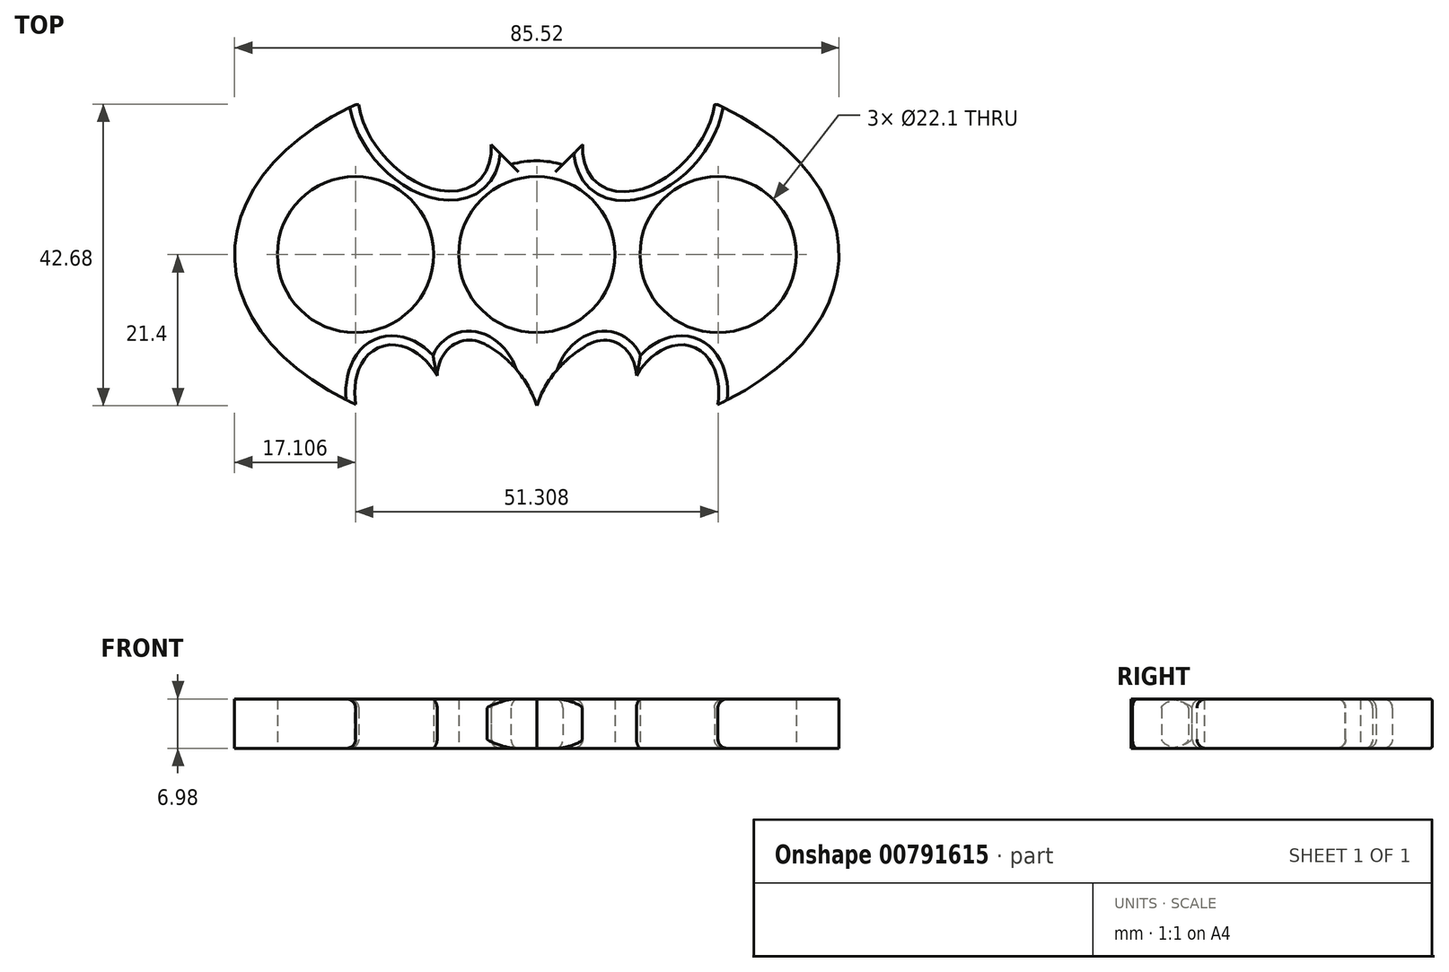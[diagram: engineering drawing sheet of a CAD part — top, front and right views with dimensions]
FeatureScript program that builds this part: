
annotation { "Feature Type Name" : "Feature", "Feature Type Description" : "" }
export const myFeature = defineFeature(function(context is Context, id is Id, definition is map)
    precondition{}
    {
        {
            var Q0;
            Q0=qCreatedBy(makeId("Top.planeOp"),FACE);
            var sketch = newSketch(context, id + "F0", { "sketchPlane" : qUnion([Q0])});
            skCircle(sketch, "E0", {"center": v(0, 0) * mm, "radius": 11.05 * mm});
            skCircle(sketch, "E1", {"center": v(25.65, 0) * mm, "radius": 11.05 * mm});
            skCircle(sketch, "E2", {"center": v(-25.65, 0) * mm, "radius": 11.05 * mm});
            skEllipse(sketch, "E3", {"center": v(0, 0) * mm, "majorRadius": 42.76 * mm, "minorRadius": 26.5 * mm, "majorAxis": v(1, 0)});
            skPoint(sketch, "E4", {"position": v(0, 11.05) * mm});
            skPoint(sketch, "E5", {"position": v(-25.65, 21.2) * mm});
            skLineSegment(sketch, "E6", {"start": v(-25.65, 21.2) * mm, "end": v(25.65, 21.2) * mm});
            skPoint(sketch, "E7", {"position": v(0, 21.2) * mm});
            skPoint(sketch, "E8", {"position": v(-24.47, -10.99) * mm});
            skPoint(sketch, "E9", {"position": v(1.18, -10.99) * mm});
            skPoint(sketch, "E10", {"position": v(26.84, -10.99) * mm});
            skLineSegment(sketch, "E11", {"start": v(-24.47, -10.99) * mm, "end": v(1.18, -10.99) * mm});
            skLineSegment(sketch, "E12", {"start": v(26.84, -10.99) * mm, "end": v(1.18, -10.99) * mm});
            skLineSegment(sketch, "E13", {"start": v(0, 0) * mm, "end": v(-19.73, 23.51) * mm});
            skLineSegment(sketch, "E14", {"start": v(0, 0) * mm, "end": v(19.73, 23.51) * mm});
            skEllipse(sketch, "E15", {"center": v(-15.88, 18.92) * mm, "majorRadius": 11.43 * mm, "minorRadius": 7.62 * mm, "majorAxis": v(0.66, -0.75)});
            skPoint(sketch, "E16", {"position": v(15.87, 18.92) * mm});
            skEllipse(sketch, "E17", {"center": v(15.87, 18.92) * mm, "majorRadius": 11.43 * mm, "minorRadius": 7.62 * mm, "majorAxis": v(-0.64, -0.77)});
            skCircle(sketch, "E18", {"center": v(0, 0) * mm, "radius": 13.26 * mm});
            skLineSegment(sketch, "E19", {"start": v(-6.43, 15.55) * mm, "end": v(6.5, 15.55) * mm});
            skLineSegment(sketch, "E20", {"start": v(-6.43, 15.55) * mm, "end": v(-3.63, 12.76) * mm});
            skLineSegment(sketch, "E21", {"start": v(6.5, 15.55) * mm, "end": v(3.69, 12.74) * mm});
            skLineSegment(sketch, "E22", {"start": v(-25.24, 21.4) * mm, "end": v(0, 21.4) * mm});
            skLineSegment(sketch, "E23", {"start": v(0, 26.5) * mm, "end": v(-1.53, 26.5) * mm});
            skPoint(sketch, "E24", {"position": v(0, -21.4) * mm});
            skLineSegment(sketch, "E25", {"start": v(0, -26.5) * mm, "end": v(1.19, -26.5) * mm});
            skLineSegment(sketch, "E26", {"start": v(0, -21.4) * mm, "end": v(-25.24, -21.4) * mm});
            skLineSegment(sketch, "E27", {"start": v(-25.24, -21.4) * mm, "end": v(0, -21.4) * mm});
            skLineSegment(sketch, "E28", {"start": v(25.24, -21.4) * mm, "end": v(0, -21.4) * mm});
            skEllipse(sketch, "E29", {"center": v(-19.05, -21.4) * mm, "majorRadius": 8.9 * mm, "minorRadius": 6.35 * mm, "majorAxis": v(0.34, -0.94)});
            skEllipse(sketch, "E30", {"center": v(-8.9, -18.35) * mm, "majorRadius": 6.35 * mm, "minorRadius": 5.08 * mm, "majorAxis": v(0.3, -0.95)});
            skArc(sketch, "E31", {"start": v(0, -21.4) * mm, "mid": v(-2.93, -16.21) * mm, "end": v(-7.62, -12.55) * mm});
            skEllipse(sketch, "E32", {"center": v(8.89, -18.35) * mm, "majorRadius": 6.35 * mm, "minorRadius": 5.08 * mm, "majorAxis": v(0.3, 0.95)});
            skEllipse(sketch, "E33", {"center": v(19.05, -21.4) * mm, "majorRadius": 8.9 * mm, "minorRadius": 6.35 * mm, "majorAxis": v(0.34, 0.94)});
            skArc(sketch, "E34", {"start": v(6.41, -13.3) * mm, "mid": v(2.5, -16.78) * mm, "end": v(0, -21.4) * mm});
            skLineSegment(sketch, "E35", {"start": v(19.05, -21.4) * mm, "end": v(22.1, -13.04) * mm});
            skLineSegment(sketch, "E36", {"start": v(-8.9, -18.35) * mm, "end": v(8.9, -18.35) * mm});
            skLineSegment(sketch, "E37", {"start": v(-8.9, -18.35) * mm, "end": v(-10.85, -12.3) * mm});
            skLineSegment(sketch, "E38", {"start": v(8.9, -18.35) * mm, "end": v(10.85, -12.3) * mm});
            skLineSegment(sketch, "E39", {"start": v(-19.05, -21.4) * mm, "end": v(-22.1, -13.04) * mm});
            skSolve(sketch);
        }
        {
            var Q0;
            Q0=makeQuery(id+"F0.imprint","IMPRINT",FACE,{"disambiguationData":[TD([[makeQuery(id+"F0.imprint","IMPRINT",EDGE,{"derivedFrom":sQuery(id+"F0.wireOp",EDGE,"E2")}),-1.0]])]});
            var Q1;
            {var subQ5=sQuery(id+"F0.wireOp",EDGE,"E20");Q1=makeQuery(id+"F0.imprint","IMPRINT",FACE,{"disambiguationData":[TD([[makeQuery(id+"F0.imprint","IMPRINT",EDGE,{"derivedFrom":subQ5}),-1.0]])]});}
            var Q2;
            {var subQ4=sQuery(id+"F0.wireOp",EDGE,"E0");var subQ6=sQuery(id+"F0.wireOp",EDGE,"E13");var subQ7=makeQuery(id+"F0.imprint","INTERSECT",VERTEX,{"derivedFrom":[subQ4,subQ6]});Q2=makeQuery(id+"F0.imprint","IMPRINT",FACE,{"disambiguationData":[TD([[makeQuery(id+"F0.imprint","IMPRINT",EDGE,{"disambiguationData":[TD([[subQ7,1.0]])],"derivedFrom":subQ4}),-1.0]])]});}
            var Q3;
            {var subQ0=sQuery(id+"F0.wireOp",EDGE,"E11");var subQ1=sQuery(id+"F0.wireOp",EDGE,"E0");var subQ2=makeQuery(id+"F0.imprint","INTERSECT",VERTEX,{"derivedFrom":[subQ1,subQ0]});Q3=makeQuery(id+"F0.imprint","IMPRINT",FACE,{"disambiguationData":[TD([[makeQuery(id+"F0.imprint","IMPRINT",EDGE,{"disambiguationData":[TD([[subQ2,1.0]])],"derivedFrom":subQ1}),-1.0]])]});}
            var Q4;
            {var subQ5=sQuery(id+"F0.wireOp",EDGE,"E21");Q4=makeQuery(id+"F0.imprint","IMPRINT",FACE,{"disambiguationData":[TD([[makeQuery(id+"F0.imprint","IMPRINT",EDGE,{"derivedFrom":subQ5}),1.0]])]});}
            var Q5;
            {var subQ0=sQuery(id+"F0.wireOp",EDGE,"E12");var subQ1=sQuery(id+"F0.wireOp",EDGE,"E0");var subQ2=makeQuery(id+"F0.imprint","INTERSECT",VERTEX,{"derivedFrom":[subQ1,subQ0]});Q5=makeQuery(id+"F0.imprint","IMPRINT",FACE,{"disambiguationData":[TD([[makeQuery(id+"F0.imprint","IMPRINT",EDGE,{"disambiguationData":[TD([[subQ2,-1.0]])],"derivedFrom":subQ1}),-1.0]])]});}
            var Q6;
            {var subQ0=sQuery(id+"F0.wireOp",EDGE,"E11");var subQ1=sQuery(id+"F0.wireOp",EDGE,"E0");var subQ2=makeQuery(id+"F0.imprint","INTERSECT",VERTEX,{"derivedFrom":[subQ1,subQ0]});Q6=makeQuery(id+"F0.imprint","IMPRINT",FACE,{"disambiguationData":[TD([[makeQuery(id+"F0.imprint","IMPRINT",EDGE,{"disambiguationData":[TD([[subQ2,-1.0]])],"derivedFrom":subQ1}),-1.0]])]});}
            var Q7;
            {var subQ1=sQuery(id+"F0.wireOp",EDGE,"E31");var subQ3=sQuery(id+"F0.wireOp",EDGE,"E36");var subQ4=makeQuery(id+"F0.imprint","INTERSECT",VERTEX,{"derivedFrom":[subQ1,subQ3]});Q7=makeQuery(id+"F0.imprint","IMPRINT",FACE,{"disambiguationData":[TD([[makeQuery(id+"F0.imprint","IMPRINT",EDGE,{"disambiguationData":[TD([[subQ4,-1.0]])],"derivedFrom":subQ3}),-1.0]])]});}
            extrude(context, id + "F1", {"entities" : qUnion([Q0, Q1, Q2, Q3, Q4, Q5, Q6, Q7]), "endBound" : BoundingType.SYMMETRIC, "depth" : 7 * mm, "offsetDistance" : 25.4 * mm});
        }
        {
            var Q0;
            Q0=makeQuery(id+"F1.opExtrude","CAP_EDGE",EDGE,{"disambiguationData":[OSD([sQuery(id+"F0.wireOp",EDGE,"E15")])],"isStart":false});
            var Q1;
            Q1=makeQuery(id+"F1.opExtrude","CAP_EDGE",EDGE,{"disambiguationData":[OSD([sQuery(id+"F0.wireOp",EDGE,"E17")])],"isStart":false});
            var Q2;
            Q2=makeQuery(id+"F1.opExtrude","CAP_EDGE",EDGE,{"disambiguationData":[OSD([sQuery(id+"F0.wireOp",EDGE,"E18")])],"isStart":false});
            var Q3;
            Q3=makeQuery(id+"F1.opExtrude","CAP_EDGE",EDGE,{"disambiguationData":[OSD([sQuery(id+"F0.wireOp",EDGE,"E32")])],"isStart":false});
            var Q4;
            Q4=makeQuery(id+"F1.opExtrude","CAP_EDGE",EDGE,{"disambiguationData":[OSD([sQuery(id+"F0.wireOp",EDGE,"E33")])],"isStart":false});
            var Q5;
            Q5=makeQuery(id+"F1.opExtrude","CAP_EDGE",EDGE,{"disambiguationData":[OSD([sQuery(id+"F0.wireOp",EDGE,"E30")])],"isStart":false});
            var Q6;
            Q6=makeQuery(id+"F1.opExtrude","CAP_EDGE",EDGE,{"disambiguationData":[OSD([sQuery(id+"F0.wireOp",EDGE,"E29")])],"isStart":false});
            var Q7;
            Q7=makeQuery(id+"F1.opExtrude","CAP_EDGE",EDGE,{"disambiguationData":[OSD([sQuery(id+"F0.wireOp",EDGE,"E18")])],"isStart":true});
            var Q8;
            Q8=makeQuery(id+"F1.opExtrude","CAP_EDGE",EDGE,{"disambiguationData":[OSD([sQuery(id+"F0.wireOp",EDGE,"E17")])],"isStart":true});
            var Q9;
            Q9=makeQuery(id+"F1.opExtrude","CAP_EDGE",EDGE,{"disambiguationData":[OSD([sQuery(id+"F0.wireOp",EDGE,"E15")])],"isStart":true});
            var Q10;
            Q10=makeQuery(id+"F1.opExtrude","CAP_EDGE",EDGE,{"disambiguationData":[OSD([sQuery(id+"F0.wireOp",EDGE,"E33")])],"isStart":true});
            var Q11;
            Q11=makeQuery(id+"F1.opExtrude","CAP_EDGE",EDGE,{"disambiguationData":[OSD([sQuery(id+"F0.wireOp",EDGE,"E32")])],"isStart":true});
            var Q12;
            Q12=makeQuery(id+"F1.opExtrude","CAP_EDGE",EDGE,{"disambiguationData":[OSD([sQuery(id+"F0.wireOp",EDGE,"E30")])],"isStart":true});
            var Q13;
            Q13=makeQuery(id+"F1.opExtrude","CAP_EDGE",EDGE,{"disambiguationData":[OSD([sQuery(id+"F0.wireOp",EDGE,"E29")])],"isStart":true});
            fillet(context, id + "F2", {"entities" : qUnion([Q0, Q1, Q2, Q3, Q4, Q5, Q6, Q7, Q8, Q9, Q10, Q11, Q12, Q13]), "radius" : 1.27 * mm, "tangentPropagation" : true, "allowEdgeOverflow" : false});
        }
    });
